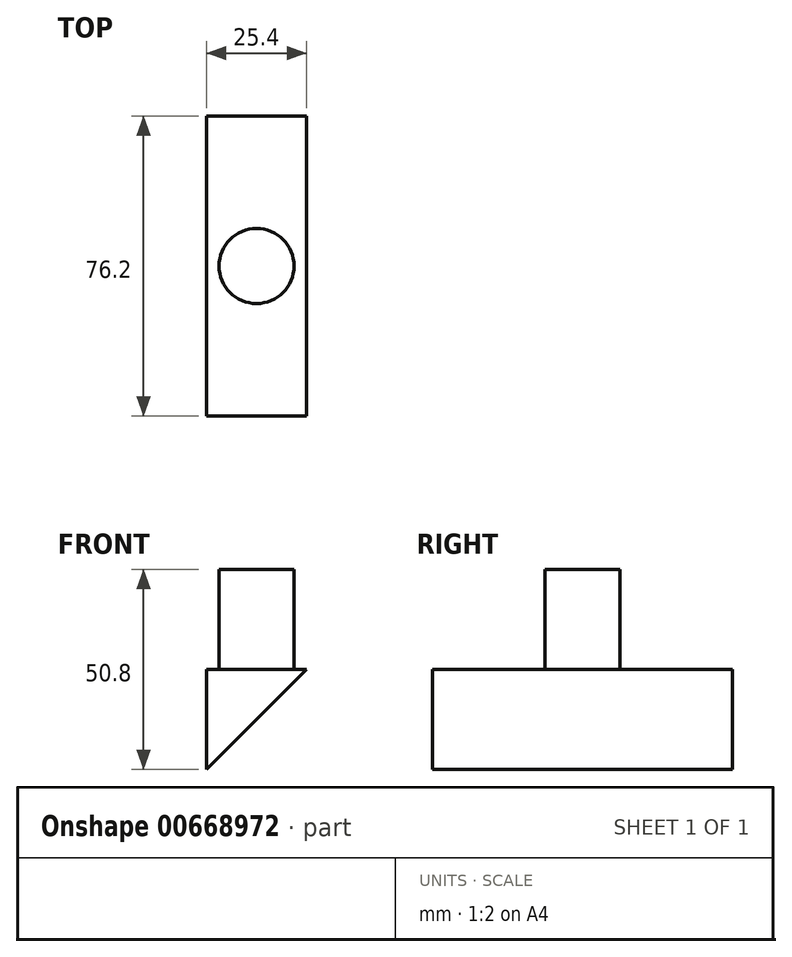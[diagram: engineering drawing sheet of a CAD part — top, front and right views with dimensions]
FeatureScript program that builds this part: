
annotation { "Feature Type Name" : "Feature", "Feature Type Description" : "" }
export const myFeature = defineFeature(function(context is Context, id is Id, definition is map)
    precondition{}
    {
        {
            var Q0;
            Q0=qCreatedBy(makeId("Top.planeOp"),FACE);
            var sketch = newSketch(context, id + "F0", { "sketchPlane" : qUnion([Q0])});
            skCircle(sketch, "E0", {"center": v(0, 0) * mm, "radius": 9.53 * mm});
            skSolve(sketch);
        }
        {
            var Q0;
            Q0 = qSketchRegion(id + "F0", true);
            extrude(context, id + "F1", {"entities" : qUnion([Q0]), "depth" : 25.4 * mm, "offsetDistance" : 25.4 * mm});
        }
        {
            var Q0;
            Q0=makeQuery(id+"F1.opExtrude","CAP_FACE",FACE,{"disambiguationData":[OSD([sQuery(id+"F0.wireOp",EDGE,"E0")])],"isStart":true});
            var sketch = newSketch(context, id + "F2", { "sketchPlane" : qUnion([Q0])});
            skLineSegment(sketch, "E1.bottom", {"start": v(-12.7, 38.1) * mm, "end": v(12.7, 38.1) * mm});
            skLineSegment(sketch, "E1.top", {"start": v(-12.7, -38.1) * mm, "end": v(12.7, -38.1) * mm});
            skLineSegment(sketch, "E1.left", {"start": v(-12.7, 38.1) * mm, "end": v(-12.7, -38.1) * mm});
            skLineSegment(sketch, "E1.right", {"start": v(12.7, 38.1) * mm, "end": v(12.7, -38.1) * mm});
            skSolve(sketch);
        }
        {
            var Q0;
            Q0 = qSketchRegion(id + "F2", true);
            extrude(context, id + "F3", {"entities" : qUnion([Q0]), "operationType" : NewBodyOperationType.ADD, "depth" : 25.4 * mm, "offsetDistance" : 25.4 * mm});
        }
        {
            var Q0;
            Q0=makeQuery(id+"F3.opExtrude","SWEPT_FACE",FACE,{"disambiguationData":[OSD([sQuery(id+"F2.wireOp",EDGE,"E1.bottom")])]});
            var sketch = newSketch(context, id + "F4", { "sketchPlane" : qUnion([Q0])});
            skLineSegment(sketch, "E2", {"start": v(12.7, 0) * mm, "end": v(-12.7, -25.4) * mm});
            skLineSegment(sketch, "E3", {"start": v(-12.7, -25.4) * mm, "end": v(12.7, -25.4) * mm});
            skLineSegment(sketch, "E4", {"start": v(12.7, -25.4) * mm, "end": v(12.7, 0) * mm});
            skSolve(sketch);
        }
        {
            var Q0;
            Q0 = qSketchRegion(id + "F4", true);
            extrude(context, id + "F5", {"entities" : qUnion([Q0]), "operationType" : NewBodyOperationType.REMOVE, "endBound" : BoundingType.THROUGH_ALL, "oppositeDirection" : true, "depth" : 25.4 * mm, "offsetDistance" : 25.4 * mm});
        }
    });
